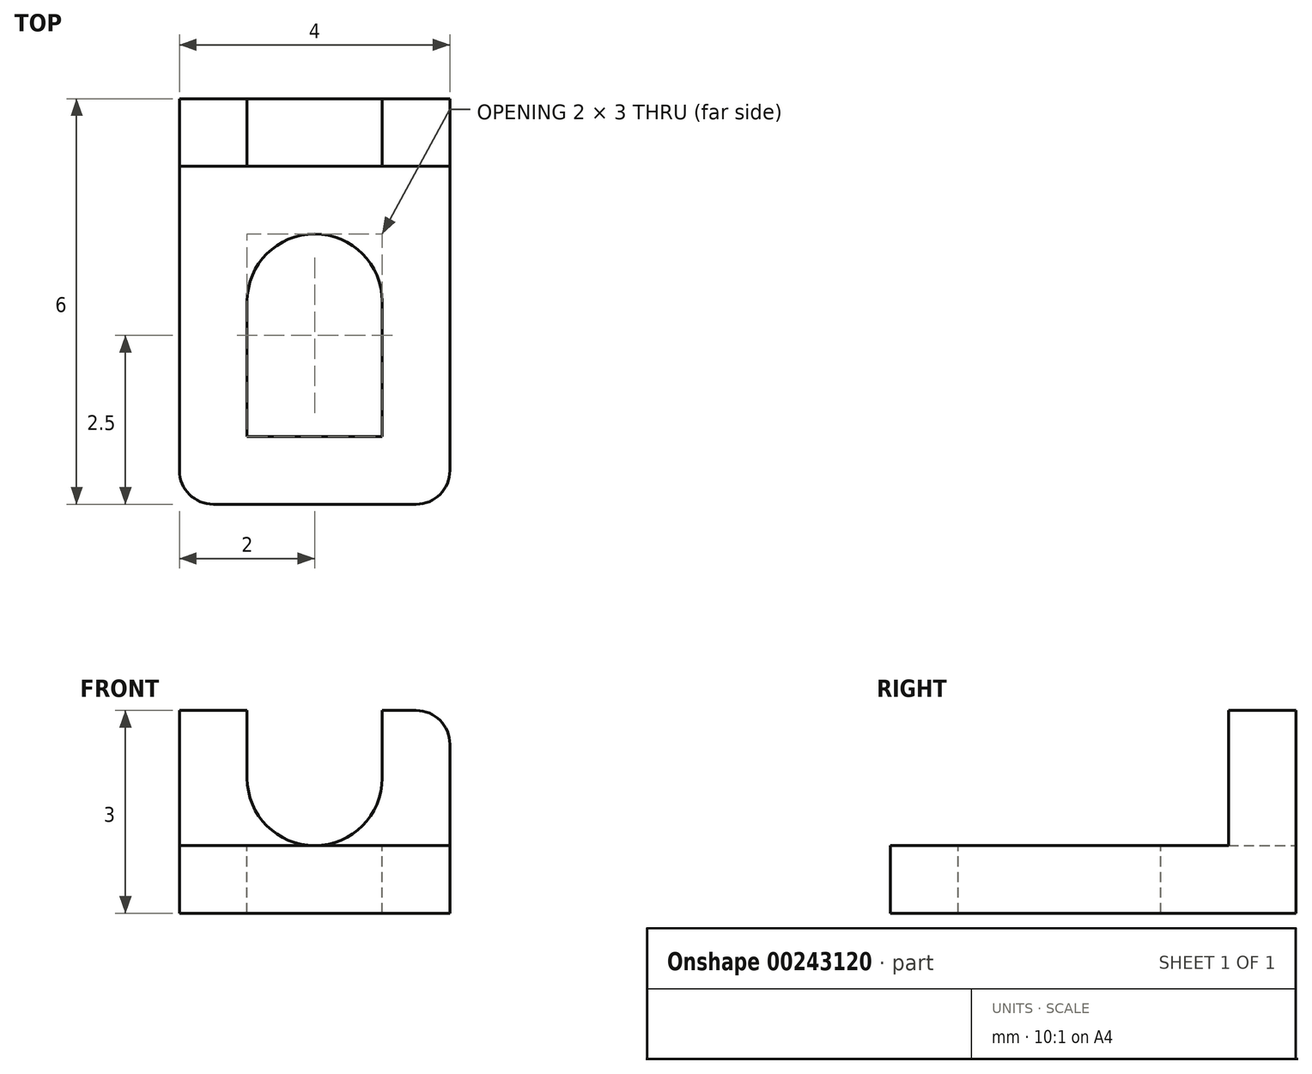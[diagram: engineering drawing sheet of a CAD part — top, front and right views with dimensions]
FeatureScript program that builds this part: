
annotation { "Feature Type Name" : "Feature", "Feature Type Description" : "" }
export const myFeature = defineFeature(function(context is Context, id is Id, definition is map)
    precondition{}
    {
        {
            var Q0;
            Q0=qCreatedBy(makeId("Front.planeOp"),FACE);
            var sketch = newSketch(context, id + "F0", { "sketchPlane" : qUnion([Q0])});
            skLineSegment(sketch, "E0", {"start": v(0, 0) * mm, "end": v(4, 0) * mm});
            skLineSegment(sketch, "E1", {"start": v(4, 0) * mm, "end": v(4, 3) * mm});
            skLineSegment(sketch, "E2", {"start": v(4, 3) * mm, "end": v(0, 3) * mm});
            skLineSegment(sketch, "E3", {"start": v(0, 3) * mm, "end": v(0, 0) * mm});
            skSolve(sketch);
        }
        {
            var Q0;
            Q0 = qSketchRegion(id + "F0", true);
            extrude(context, id + "F1", {"entities" : qUnion([Q0]), "depth" : 6 * mm});
        }
        {
            var Q0;
            Q0=makeQuery(id+"F1.opExtrude","CAP_EDGE",EDGE,{"disambiguationData":[OSD([sQuery(id+"F0.wireOp",EDGE,"E1")])],"isStart":false});
            fillet(context, id + "F2", {"entities" : qUnion([Q0]), "radius" : 0.5 * mm, "tangentPropagation" : true, "allowEdgeOverflow" : false});
        }
        {
            var Q0;
            Q0=makeQuery(id+"F1.opExtrude","CAP_EDGE",EDGE,{"disambiguationData":[OSD([sQuery(id+"F0.wireOp",EDGE,"E3")])],"isStart":false});
            fillet(context, id + "F3", {"entities" : qUnion([Q0]), "radius" : 0.5 * mm, "tangentPropagation" : true, "allowEdgeOverflow" : false});
        }
        {
            var Q0;
            Q0=makeQuery(id+"F1.opExtrude","CAP_FACE",FACE,{"disambiguationData":[OSD([sQuery(id+"F0.wireOp",EDGE,"E0"),sQuery(id+"F0.wireOp",EDGE,"E1"),sQuery(id+"F0.wireOp",EDGE,"E2"),sQuery(id+"F0.wireOp",EDGE,"E3")])],"isStart":true});
            var sketch = newSketch(context, id + "F4", { "sketchPlane" : qUnion([Q0])});
            skLineSegment(sketch, "E4", {"start": v(0, 3) * mm, "end": v(-1, 3) * mm});
            skLineSegment(sketch, "E5", {"start": v(-1, 3) * mm, "end": v(-1, 2) * mm});
            skLineSegment(sketch, "E6", {"start": v(-1, 2) * mm, "end": v(-2, 2) * mm});
            skCircle(sketch, "E7", {"center": v(-2, 2) * mm, "radius": 1 * mm});
            skLineSegment(sketch, "E8", {"start": v(-2, 2) * mm, "end": v(-3, 2) * mm});
            skLineSegment(sketch, "E9", {"start": v(-3, 2) * mm, "end": v(-3, 3) * mm});
            skSolve(sketch);
        }
        {
            var Q0;
            Q0 = qSketchRegion(id + "F4", true);
            var Q1;
            {var subQ0=sQuery(id+"F4.wireOp",EDGE,"E9");Q1=makeQuery(id+"F4.imprint","IMPRINT",FACE,{"disambiguationData":[TD([[makeQuery(id+"F4.imprint","IMPRINT",EDGE,{"derivedFrom":subQ0}),-1.0]])]});}
            var Q2;
            {var subQ0=sQuery(id+"F4.wireOp",EDGE,"E5");Q2=makeQuery(id+"F4.imprint","IMPRINT",FACE,{"disambiguationData":[TD([[makeQuery(id+"F4.imprint","IMPRINT",EDGE,{"derivedFrom":subQ0}),-1.0]])]});}
            extrude(context, id + "F5", {"entities" : qUnion([Q0, Q1, Q2]), "operationType" : NewBodyOperationType.REMOVE, "oppositeDirection" : true, "depth" : 25 * mm});
        }
        {
            var Q0;
            {var subQ0=sQuery(id+"F0.wireOp",EDGE,"E1");var subQ2=sQuery(id+"F0.wireOp",EDGE,"E2");Q0=makeQuery(id+"F5.boolean.opBoolean","SPLIT",FACE,{"disambiguationData":[TD([makeQuery(id+"F1.opExtrude","SWEPT_FACE",FACE,{"disambiguationData":[OSD([subQ0])]})])],"derivedFrom":makeQuery(id+"F1.opExtrude","SWEPT_FACE",FACE,{"disambiguationData":[OSD([subQ2])]})});}
            var sketch = newSketch(context, id + "F6", { "sketchPlane" : qUnion([Q0])});
            skLineSegment(sketch, "E10", {"start": v(4, 0) * mm, "end": v(4, -1) * mm});
            skLineSegment(sketch, "E11", {"start": v(4, -1) * mm, "end": v(0, -1) * mm});
            skLineSegment(sketch, "E12", {"start": v(4, -1) * mm, "end": v(4, -6.81) * mm});
            skLineSegment(sketch, "E13", {"start": v(4, -6.81) * mm, "end": v(0, -6.81) * mm});
            skLineSegment(sketch, "E14", {"start": v(0, -6.81) * mm, "end": v(0, -1) * mm});
            skSolve(sketch);
        }
        {
            var Q0;
            Q0 = qSketchRegion(id + "F6", true);
            extrude(context, id + "F7", {"entities" : qUnion([Q0]), "operationType" : NewBodyOperationType.REMOVE, "oppositeDirection" : true, "depth" : 2 * mm});
        }
        {
            var Q0;
            Q0=makeQuery(id+"F1.opExtrude","SWEPT_EDGE",EDGE,{"disambiguationData":[OSD([sQuery(id+"F0.wireOp",EDGE,"E1"),sQuery(id+"F0.wireOp",EDGE,"E2")])]});
            fillet(context, id + "F8", {"entities" : qUnion([Q0]), "radius" : 0.5 * mm, "tangentPropagation" : true, "allowEdgeOverflow" : false});
        }
        {
            var Q0;
            Q0=makeQuery(id+"F7.boolean.opBoolean","COPY",FACE,{"derivedFrom":makeQuery(id+"F7.opExtrude","CAP_FACE",FACE,{"disambiguationData":[OSD([sQuery(id+"F6.wireOp",EDGE,"E11"),sQuery(id+"F6.wireOp",EDGE,"E12"),sQuery(id+"F6.wireOp",EDGE,"E13"),sQuery(id+"F6.wireOp",EDGE,"E14")])],"isStart":false})});
            var sketch = newSketch(context, id + "F9", { "sketchPlane" : qUnion([Q0])});
            skCircle(sketch, "E15", {"center": v(2, -3) * mm, "radius": 1 * mm});
            skLineSegment(sketch, "E16", {"start": v(3, -3) * mm, "end": v(3, -6) * mm});
            skLineSegment(sketch, "E17", {"start": v(1, -3) * mm, "end": v(1, -6) * mm});
            skLineSegment(sketch, "E18", {"start": v(1, -6) * mm, "end": v(1, -5) * mm});
            skLineSegment(sketch, "E19", {"start": v(1, -5) * mm, "end": v(3, -5) * mm});
            skSolve(sketch);
        }
        {
            var Q0;
            Q0 = qSketchRegion(id + "F9", true);
            extrude(context, id + "F10", {"entities" : qUnion([Q0]), "operationType" : NewBodyOperationType.REMOVE, "oppositeDirection" : true, "depth" : 25 * mm});
        }
    });
